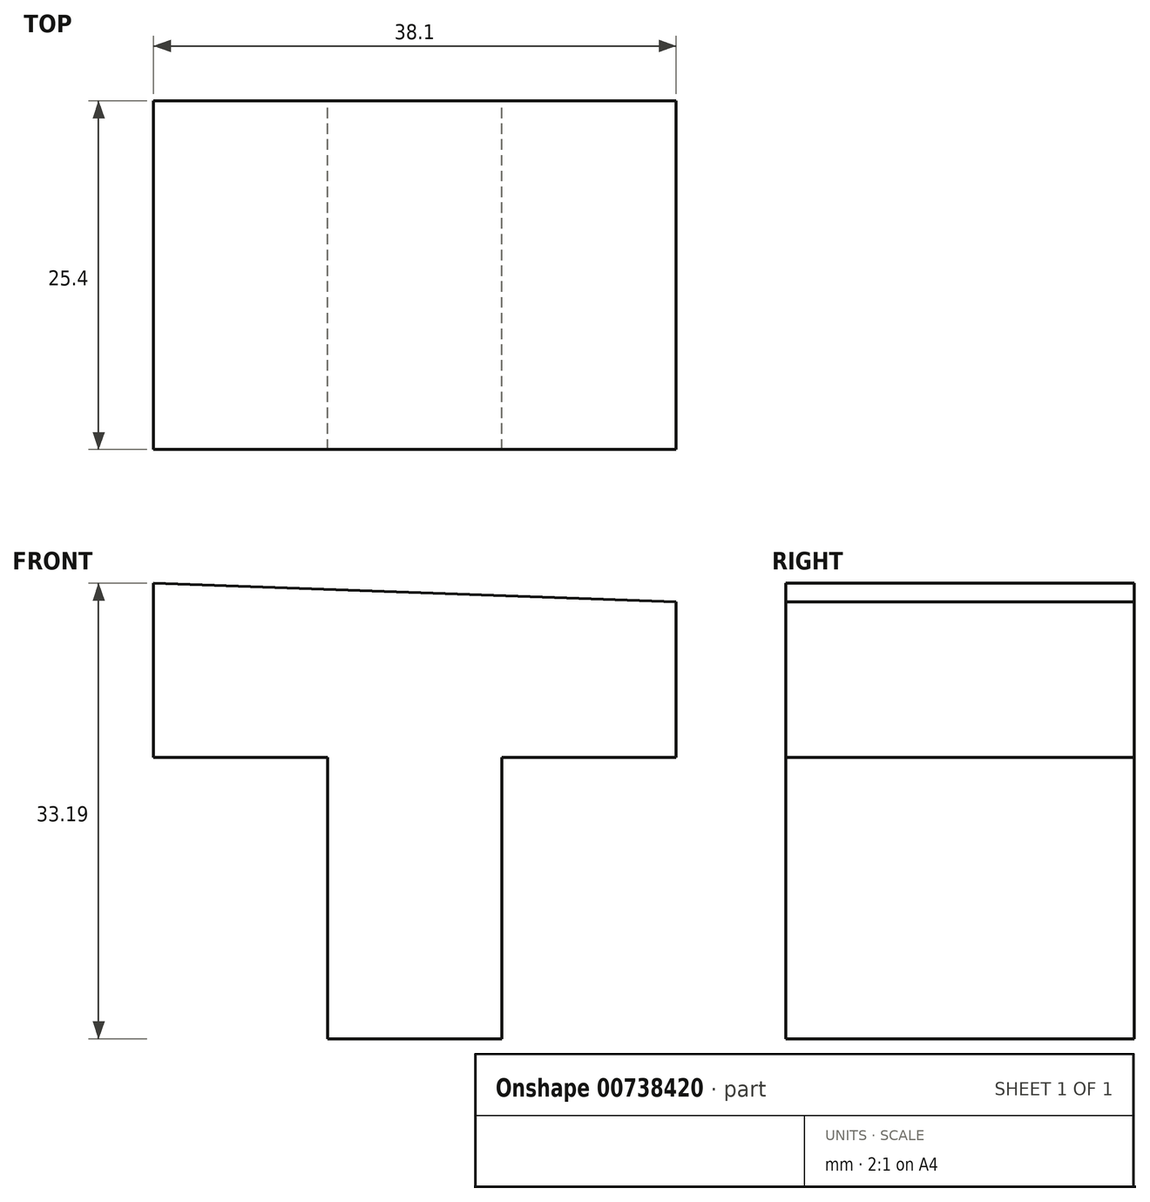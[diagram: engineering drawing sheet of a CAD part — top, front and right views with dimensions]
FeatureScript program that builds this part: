
annotation { "Feature Type Name" : "Feature", "Feature Type Description" : "" }
export const myFeature = defineFeature(function(context is Context, id is Id, definition is map)
    precondition{}
    {
        {
            var Q0;
            Q0=qCreatedBy(makeId("Front.planeOp"),FACE);
            var sketch = newSketch(context, id + "F0", { "sketchPlane" : qUnion([Q0])});
            skLineSegment(sketch, "E0", {"start": v(0, 20.49) * mm, "end": v(0, 0) * mm});
            skLineSegment(sketch, "E1", {"start": v(0, 0) * mm, "end": v(12.7, 0) * mm});
            skLineSegment(sketch, "E2", {"start": v(12.7, 0) * mm, "end": v(12.7, 20.49) * mm});
            skLineSegment(sketch, "E3", {"start": v(12.7, 20.49) * mm, "end": v(25.4, 20.49) * mm});
            skLineSegment(sketch, "E4", {"start": v(25.4, 20.49) * mm, "end": v(25.4, 33.19) * mm});
            skLineSegment(sketch, "E5", {"start": v(25.4, 31.83) * mm, "end": v(-12.7, 33.19) * mm});
            skLineSegment(sketch, "E6", {"start": v(-12.7, 33.19) * mm, "end": v(-12.7, 20.49) * mm});
            skLineSegment(sketch, "E7", {"start": v(-12.7, 20.49) * mm, "end": v(0, 20.49) * mm});
            skSolve(sketch);
        }
        {
            var Q0;
            Q0 = qSketchRegion(id + "F0", true);
            var Q1;
            Q1=makeQuery(id+"F0.imprint","IMPRINT",FACE,{"disambiguationData":[TD([[makeQuery(id+"F0.imprint","IMPRINT",EDGE,{"derivedFrom":sQuery(id+"F0.wireOp",EDGE,"E0")}),1.0]])]});
            extrude(context, id + "F1", {"entities" : qUnion([Q0, Q1]), "depth" : 25.4 * mm, "offsetDistance" : 25.4 * mm});
        }
    });
